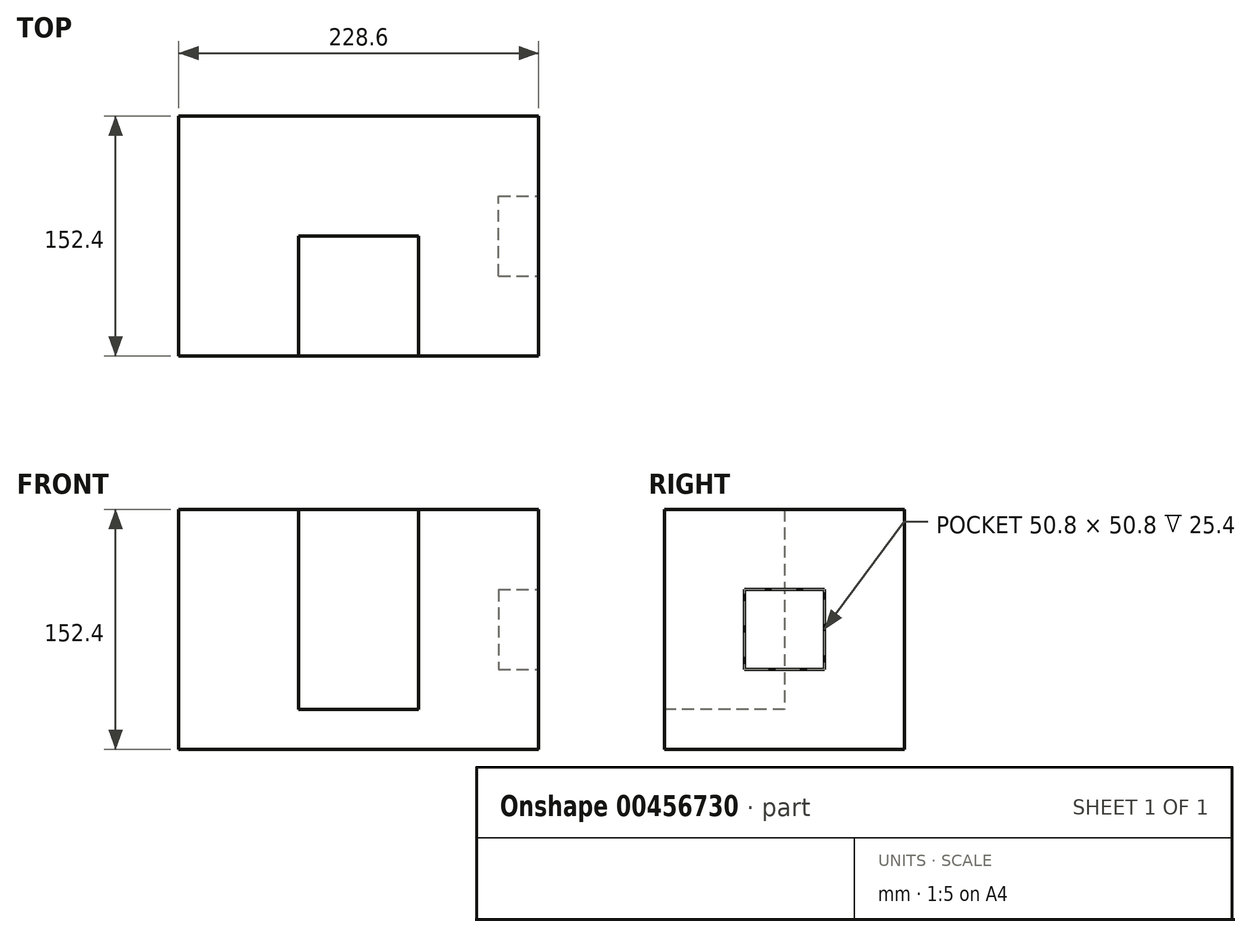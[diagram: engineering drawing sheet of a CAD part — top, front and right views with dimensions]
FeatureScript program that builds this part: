
annotation { "Feature Type Name" : "Feature", "Feature Type Description" : "" }
export const myFeature = defineFeature(function(context is Context, id is Id, definition is map)
    precondition{}
    {
        {
            var Q0;
            Q0=qCreatedBy(makeId("Front.planeOp"),FACE);
            var sketch = newSketch(context, id + "F0", { "sketchPlane" : qUnion([Q0])});
            skLineSegment(sketch, "E0", {"start": v(113.73, -108.87) * mm, "end": v(-114.87, -108.87) * mm});
            skLineSegment(sketch, "E1", {"start": v(-114.87, -108.87) * mm, "end": v(-114.87, 43.53) * mm});
            skLineSegment(sketch, "E2", {"start": v(-114.87, 43.53) * mm, "end": v(113.73, 43.53) * mm});
            skLineSegment(sketch, "E3", {"start": v(113.73, 43.53) * mm, "end": v(113.73, -108.87) * mm});
            skPoint(sketch, "E4", {"position": v(-38.67, 43.53) * mm});
            skPoint(sketch, "E5", {"position": v(37.53, 43.53) * mm});
            skSolve(sketch);
        }
        {
            var Q0;
            Q0=makeQuery(id+"F0.imprint","IMPRINT",FACE,{"disambiguationData":[TD([[makeQuery(id+"F0.imprint","IMPRINT",EDGE,{"derivedFrom":sQuery(id+"F0.wireOp",EDGE,"E0")}),-1.0]])]});
            extrude(context, id + "F1", {"entities" : qUnion([Q0]), "depth" : 152.4 * mm});
        }
        {
            var Q0;
            Q0=makeQuery(id+"F1.opExtrude","CAP_FACE",FACE,{"disambiguationData":[OSD([sQuery(id+"F0.wireOp",EDGE,"E0"),sQuery(id+"F0.wireOp",EDGE,"E1"),sQuery(id+"F0.wireOp",EDGE,"E2"),sQuery(id+"F0.wireOp",EDGE,"E3")])],"isStart":false});
            var sketch = newSketch(context, id + "F2", { "sketchPlane" : qUnion([Q0])});
            skPoint(sketch, "E6", {"position": v(-38.67, 43.53) * mm});
            skPoint(sketch, "E7", {"position": v(37.53, 43.53) * mm});
            skLineSegment(sketch, "E8", {"start": v(-38.67, 43.53) * mm, "end": v(-38.67, -83.47) * mm});
            skLineSegment(sketch, "E9", {"start": v(-38.67, -83.47) * mm, "end": v(37.53, -83.47) * mm});
            skLineSegment(sketch, "E10", {"start": v(37.53, -83.47) * mm, "end": v(37.53, 43.53) * mm});
            skSolve(sketch);
        }
        {
            var Q0;
            {var subQ0=sQuery(id+"F2.wireOp",EDGE,"E8");Q0=makeQuery(id+"F2.imprint","IMPRINT",FACE,{"disambiguationData":[TD([[makeQuery(id+"F2.imprint","IMPRINT",EDGE,{"derivedFrom":subQ0}),1.0]])]});}
            extrude(context, id + "F3", {"entities" : qUnion([Q0]), "operationType" : NewBodyOperationType.REMOVE, "oppositeDirection" : true, "depth" : 76.2 * mm});
        }
        {
            var Q0;
            Q0=makeQuery(id+"F1.opExtrude","SWEPT_FACE",FACE,{"disambiguationData":[OSD([sQuery(id+"F0.wireOp",EDGE,"E3")])]});
            var sketch = newSketch(context, id + "F4", { "sketchPlane" : qUnion([Q0])});
            skLineSegment(sketch, "E11.bottom", {"start": v(-101.6, -7.27) * mm, "end": v(-50.8, -7.27) * mm});
            skLineSegment(sketch, "E11.top", {"start": v(-101.6, -58.07) * mm, "end": v(-50.8, -58.07) * mm});
            skLineSegment(sketch, "E11.left", {"start": v(-101.6, -7.27) * mm, "end": v(-101.6, -58.07) * mm});
            skLineSegment(sketch, "E11.right", {"start": v(-50.8, -7.27) * mm, "end": v(-50.8, -58.07) * mm});
            skPoint(sketch, "E11.middle", {"position": v(-76.2, -32.67) * mm});
            skSolve(sketch);
        }
        {
            var Q0;
            Q0 = qSketchRegion(id + "F4", true);
            extrude(context, id + "F5", {"entities" : qUnion([Q0]), "operationType" : NewBodyOperationType.REMOVE, "oppositeDirection" : true, "depth" : 25.4 * mm});
        }
    });
